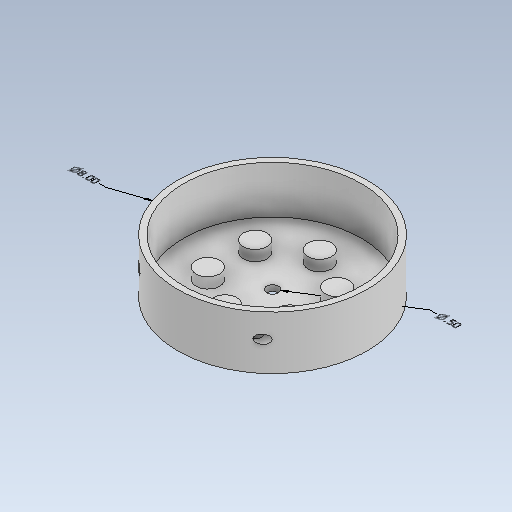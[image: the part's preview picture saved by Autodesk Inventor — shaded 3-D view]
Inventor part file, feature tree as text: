
AUTODESK INVENTOR PART (.ipt)
format: ipt  version: 2021 (Build 250183000, 183)  size: 168,448 bytes
history: native  units: in
note: dims shown in document units (in); Inventor stores cm internally (conversion verified against a paired STEP export)
features: other x6, extrude x5, sketch x5, pattern_circular x1, reference x1
ambient origin geometry x8: Origin, YZ Plane, XZ Plane, XY Plane, X Axis, Y Axis, Z Axis, Center Point
bodies: Solid1 (feature_tree)
feature tree (18):
  other  "Annotations"
  extrude  "Extrusion1"  Depth=0.25in
  extrude  "Extrusion2"  TaperAngle=0.0deg  [1 undecoded]
  extrude  "Extrusion3"  TaperAngle=0.0deg  [1 undecoded]
  extrude  "Extrusion5"  Depth=4.0in TaperAngle=0.0deg
  pattern_circular  "Circular Pattern1"  [2 undecoded]
  extrude  "Extrusion6"  [1 undecoded]
  sketch  "Sketch1"  dims[d3=0.0in d4=0.25in]
  sketch  "Sketch2"  dims[d5=8.0in d7=0.0in]
  sketch  "Sketch3"  dims[d10=2.0in d11=0.0in d25=0.0in]
  sketch  "Sketch5"  dims[d27=360.0deg d29=4.0in d30=0.0in]
  sketch  "Sketch6"  dims[d12=1.4589in d13=0.5in d31=0.129in d32=8.0in]
  reference  "Reference1"
  parser-record x1  (decoder bookkeeping rows leaked as tree rows — omitted from the tree; the rows remain in map.json)
  other  "ForkMount.iam"
  other  "12x3_8-keyedDriveShaft:1"
  other  "Diameter Dimension 1"
  other  "Diameter Dimension 2"
note: 5 required parameter values undecoded (feature->parameter linkage not recoverable at this tier; creation-order binding heuristic only, values carry confidence <= 0.55)
note: 1 file-system path scrubbed to <path> (originals preserved in map.json)
